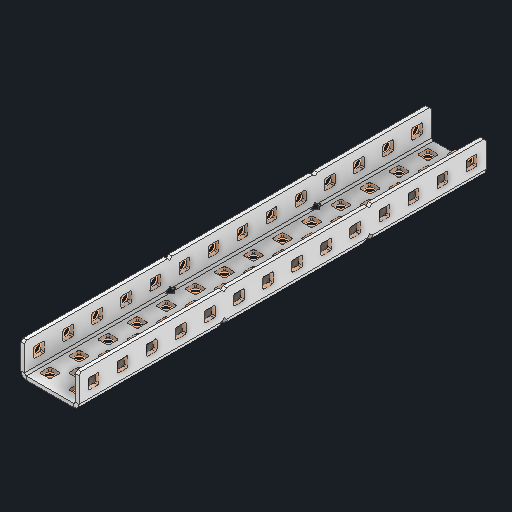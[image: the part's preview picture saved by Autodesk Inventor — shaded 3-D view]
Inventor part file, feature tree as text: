
AUTODESK INVENTOR PART (.ipt)
format: ipt  version: 2024 (Build 280153000, 153)  size: 1,022,976 bytes
history: native  units: in
note: dims shown in document units (in); Inventor stores cm internally (conversion verified against a paired STEP export)
features: other x77, extrude x68, sheet_metal_op x11, pattern_linear x2, mirror x1, chamfer x1, sketch x1
ambient origin geometry x8: Origin, YZ Plane, XZ Plane, XY Plane, X Axis, Y Axis, Z Axis, Center Point
bodies: Solid1 (feature_tree), Body (feature_tree)
feature tree (161):
  sheet_metal_op  "Flanges"
  other  "Flange Pattern Plane"
  other  "Flange Pattern Sketch"
  sheet_metal_op  "Flange Pattern"
  sheet_metal_op  "Body Pattern"
  pattern_linear  "Center Pattern"  Spacing1=7.0in  [1 undecoded]
  other  "Arc Length"
  mirror  "Notch Mirror"
  pattern_linear  "Notch Pattern"  Spacing1=0.0625in  [1 undecoded]
  chamfer  "End Chamfer"
  extrude  "Half Cut"  Depth=0.0625in
  other  "Plate1"
  sketch  "Sketch2"  dims[d0=1.0in d1=7.0in d2=0.0625in d3=0.0625in d4=0.0312in d5=0.125in d6=0.0625in d7=0.5in d8=90.0deg d9=0.0312in d10=0.25in d11=0.0625in d12=0.0625in d16=0.182in d17=0.02in d18=0.0625in d19=0.0in d20=0.25in d21=0.25in d38=5.5118in d40=0.5in d41=0.7874in d43=1.0in d46=0.172in d47=1.0in d48=0.0in d49=0.182in d50=0.02in d51=0.25in d52=0.25in d53=0.0625in d54=0.0in d55=0.172in d56=1.0in d57=0.0in d58=0.25in d60=5.5118in d62=0.5in d63=0.7874in d65=0.5in d85=0.1473in d86=0.1782in d88=0.04in d89=0.0625in d90=0.0in d91=0.04in d92=0.0491in d95=2.5in d96=0.04in d97=0.25in d98=45.0deg d99=0.25in d100=0.5in d101=0.0in d102=2.497in d106=0.182in d107=0.02in d108=0.5in d109=0.5in d110=0.0625in d111=0.0in d112=0.172in d113=0.5in d114=0.0in d117=0.5in d118=0.5in d119=0.5in]
  other  "Plate2"
  sheet_metal_op  "Bend1"
  sheet_metal_op  "Corner1"
  other  "Srf1"
  other  "Srf2"
  other  "Srf91"
  sheet_metal_op  "Body Pattern Sketch"
  other  "Srf92"
  other  "Srf786"
  other  "Srf823"
  other  "Srf824"
  other  "Srf825"
  other  "Srf826"
  other  "Srf827"
  other  "Srf828"
  other  "Srf829"
  other  "Srf856"
  other  "Srf857"
  other  "Srf858"
  other  "Srf859"
  other  "Srf860"
  other  "Srf861"
  other  "Srf862"
  other  "Srf889"
  other  "Srf890"
  other  "Srf891"
  other  "Srf892"
  other  "Srf893"
  other  "Srf894"
  other  "Srf895"
  other  "Srf896"
  other  "Srf922"
  other  "Srf923"
  other  "Srf924"
  other  "Srf925"
  other  "Srf926"
  other  "Srf959"
  other  "Srf960"
  other  "Srf961"
  other  "Srf962"
  other  "Srf963"
  other  "Srf996"
  other  "Srf997"
  other  "Srf998"
  other  "Srf999"
  other  "Srf1000"
  other  "Srf1143"
  other  "Srf1144"
  other  "Srf1145"
  other  "Srf1146"
  other  "Srf1147"
  other  "Srf1148"
  other  "Srf1149"
  other  "Srf1150"
  other  "Srf1151"
  other  "Srf1152"
  other  "Srf1153"
  other  "Srf1154"
  other  "Srf1155"
  other  "Srf1156"
  other  "Srf1199"
  other  "Srf1200"
  other  "Srf1201"
  other  "Srf1202"
  other  "Srf1203"
  other  "Srf1204"
  other  "Srf1205"
  other  "Srf1206"
  other  "Srf1207"
  other  "Srf1208"
  other  "Srf1209"
  other  "Srf1210"
  other  "Srf1211"
  other  "Srf1212"
  sheet_metal_op  "Flange Stamp"
  sheet_metal_op  "Flange Circle"
  sheet_metal_op  "Body Stamp"
  sheet_metal_op  "Body Circle"
  other  "Center Stamp"
  other  "Center Circle"
  sheet_metal_op  "Notch"
  extrude  "ExtrusionSrf2"  Depth=0.0312in
  extrude  "ExtrusionSrf92"  Depth=0.5in
  extrude  "ExtrusionSrf823"  Depth=0.0625in
  extrude  "ExtrusionSrf824"  Depth=0.5in TaperAngle=90.0deg
  extrude  "ExtrusionSrf825"  Depth=0.5in
  extrude  "ExtrusionSrf826"  Depth=0.0625in
  extrude  "ExtrusionSrf827"  Depth=0.0625in
  extrude  "ExtrusionSrf828"  Depth=0.5in
  extrude  "ExtrusionSrf829"  Depth=0.02in
  extrude  "ExtrusionSrf856"  Depth=0.0625in
  extrude  "ExtrusionSrf857"  TaperAngle=0.0deg  [1 undecoded]
  extrude  "ExtrusionSrf858"  Depth=0.5in
  extrude  "ExtrusionSrf859"  Depth=0.5in
  extrude  "ExtrusionSrf860"  Depth=0.5in
  extrude  "ExtrusionSrf861"  Depth=0.5in
  extrude  "ExtrusionSrf862"  Depth=1.0in TaperAngle=0.0deg
  extrude  "ExtrusionSrf889"  Depth=0.5in
  extrude  "ExtrusionSrf890"  Depth=0.02in
  extrude  "ExtrusionSrf891"  Depth=0.5in
  extrude  "ExtrusionSrf892"  Depth=0.5in
  extrude  "ExtrusionSrf893"  Depth=0.0625in
  extrude  "ExtrusionSrf894"  TaperAngle=0.0deg  [1 undecoded]
  extrude  "ExtrusionSrf895"  Depth=0.5in
  extrude  "ExtrusionSrf896"  Depth=1.0in TaperAngle=0.0deg
  extrude  "ExtrusionSrf922"  Depth=0.5in
  extrude  "ExtrusionSrf923"  Depth=0.5in
  extrude  "ExtrusionSrf924"  Depth=0.5in
  extrude  "ExtrusionSrf925"  Depth=0.5in
  extrude  "ExtrusionSrf926"  Depth=0.5in
  extrude  "ExtrusionSrf959"  Depth=0.5in
  extrude  "ExtrusionSrf960"  Depth=0.0625in
  extrude  "ExtrusionSrf961"  TaperAngle=0.0deg  [1 undecoded]
  extrude  "ExtrusionSrf962"  Depth=0.5in
  extrude  "ExtrusionSrf963"  Depth=0.5in
  extrude  "ExtrusionSrf996"  Depth=2.5in
  extrude  "ExtrusionSrf997"  Depth=0.5in TaperAngle=45.0deg
  extrude  "ExtrusionSrf998"  Depth=0.5in
  extrude  "ExtrusionSrf999"  Depth=0.5in TaperAngle=0.0deg
  extrude  "ExtrusionSrf1000"  Depth=0.5in
  extrude  "ExtrusionSrf1143"  Depth=0.5in
  extrude  "ExtrusionSrf1144"  Depth=0.02in
  extrude  "ExtrusionSrf1145"  Depth=0.5in
  extrude  "ExtrusionSrf1146"  Depth=0.5in
  extrude  "ExtrusionSrf1147"  Depth=0.0625in
  extrude  "ExtrusionSrf1148"  TaperAngle=0.0deg  [1 undecoded]
  extrude  "ExtrusionSrf1149"  Depth=0.5in
  extrude  "ExtrusionSrf1150"  Depth=0.5in TaperAngle=0.0deg
  extrude  "ExtrusionSrf1151"  Depth=0.5in
  extrude  "ExtrusionSrf1152"  Depth=0.5in
  extrude  "ExtrusionSrf1153"  Depth=0.5in
  extrude  "ExtrusionSrf1154"  [1 undecoded]
  extrude  "ExtrusionSrf1155"  [1 undecoded]
  extrude  "ExtrusionSrf1156"  [1 undecoded]
  extrude  "ExtrusionSrf1199"  [1 undecoded]
  extrude  "ExtrusionSrf1200"  [1 undecoded]
  extrude  "ExtrusionSrf1201"  [1 undecoded]
  extrude  "ExtrusionSrf1202"  [1 undecoded]
  extrude  "ExtrusionSrf1203"  [1 undecoded]
  extrude  "ExtrusionSrf1204"  [1 undecoded]
  extrude  "ExtrusionSrf1205"  [1 undecoded]
  extrude  "ExtrusionSrf1206"  [1 undecoded]
  extrude  "ExtrusionSrf1207"  [1 undecoded]
  extrude  "ExtrusionSrf1208"  [1 undecoded]
  extrude  "ExtrusionSrf1209"  [1 undecoded]
  extrude  "ExtrusionSrf1210"  [1 undecoded]
  extrude  "ExtrusionSrf1211"  [1 undecoded]
  extrude  "ExtrusionSrf1212"  [1 undecoded]
note: 23 required parameter values undecoded (feature->parameter linkage not recoverable at this tier; creation-order binding heuristic only, values carry confidence <= 0.55)
